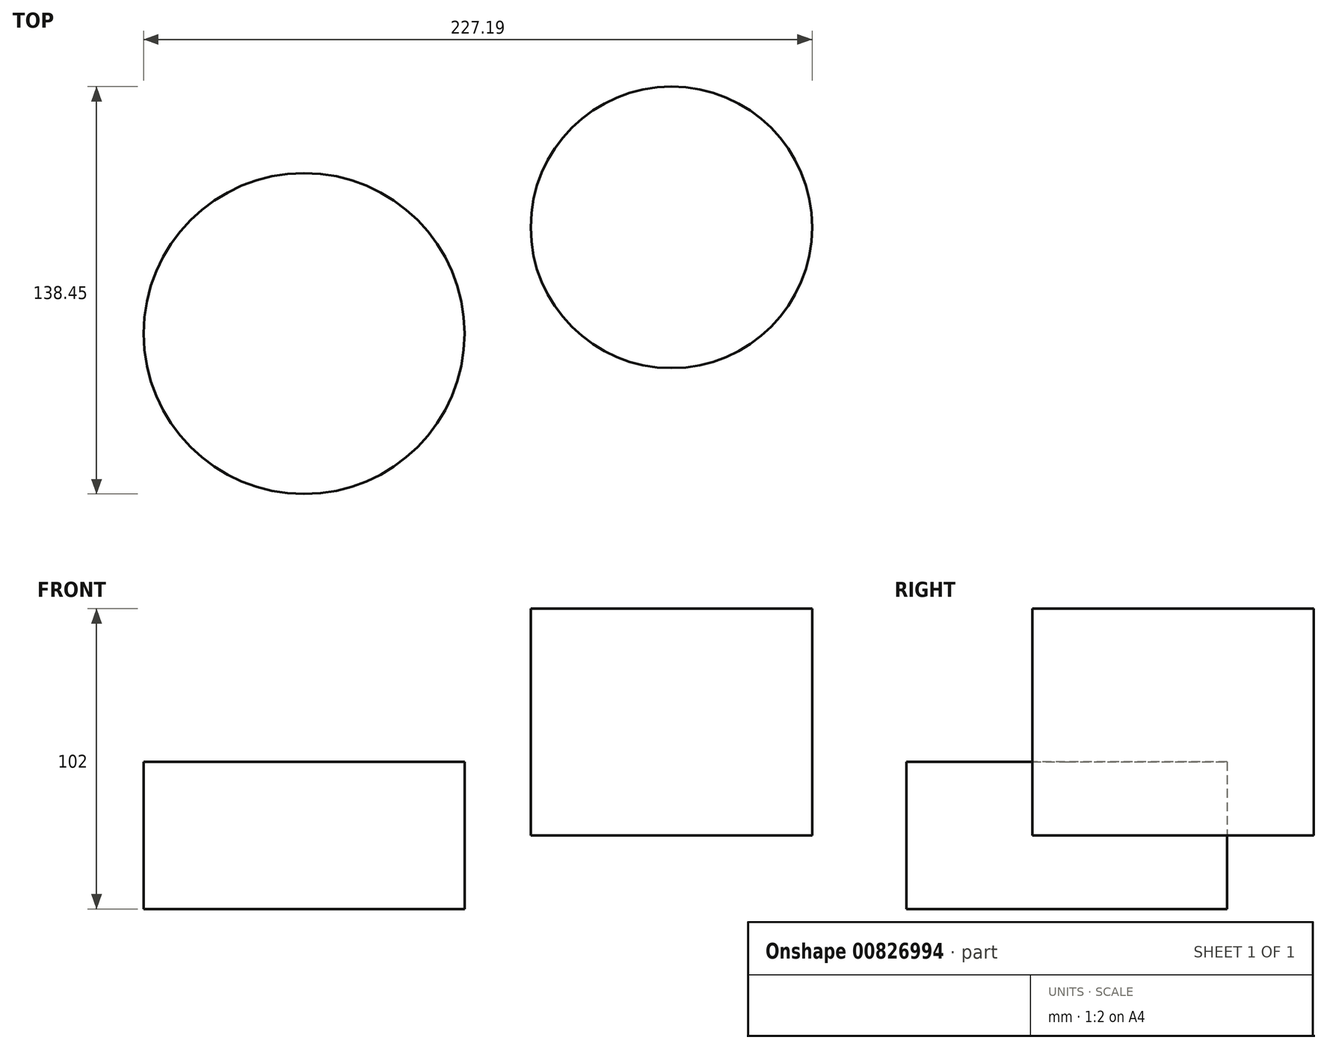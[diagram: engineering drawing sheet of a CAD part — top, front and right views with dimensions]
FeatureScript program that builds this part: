
annotation { "Feature Type Name" : "Feature", "Feature Type Description" : "" }
export const myFeature = defineFeature(function(context is Context, id is Id, definition is map)
    precondition{}
    {
        {
            var Q0;
            Q0=qCreatedBy(makeId("Top.planeOp"),FACE);
            var sketch = newSketch(context, id + "F0", { "sketchPlane" : qUnion([Q0])});
            skCircle(sketch, "E0", {"center": v(0, 0) * mm, "radius": 47.83 * mm});
            skSolve(sketch);
        }
        {
            var Q0;
            Q0=makeQuery(id+"F0.imprint","IMPRINT",FACE,{"disambiguationData":[TD([[makeQuery(id+"F0.imprint","IMPRINT",EDGE,{"derivedFrom":sQuery(id+"F0.wireOp",EDGE,"E0")}),1.0]])]});
            extrude(context, id + "F1", {"entities" : qUnion([Q0]), "depth" : 25 * mm, "offsetDistance" : 25 * mm});
        }
        {
            var Q0;
            Q0=qCreatedBy(makeId("Top.planeOp"),FACE);
            var sketch = newSketch(context, id + "F2", { "sketchPlane" : qUnion([Q0])});
            skCircle(sketch, "E1", {"center": v(-124.83, -36.1) * mm, "radius": 54.52 * mm});
            skSolve(sketch);
        }
        {
            var Q0;
            Q0=makeQuery(id+"F2.imprint","IMPRINT",FACE,{"disambiguationData":[TD([[makeQuery(id+"F2.imprint","IMPRINT",EDGE,{"derivedFrom":sQuery(id+"F2.wireOp",EDGE,"E1")}),1.0]])]});
            extrude(context, id + "F3", {"entities" : qUnion([Q0]), "depth" : 25 * mm, "offsetDistance" : 25 * mm});
        }
        {
            var Q0;
            Q0=makeQuery(id+"F3.opExtrude","CAP_FACE",FACE,{"disambiguationData":[OSD([sQuery(id+"F2.wireOp",EDGE,"E1")])],"isStart":false});
            extrude(context, id + "F4", {"entities" : qUnion([Q0]), "operationType" : NewBodyOperationType.ADD, "oppositeDirection" : true, "depth" : 25 * mm, "offsetDistance" : 25 * mm});
        }
        {
            var Q0;
            Q0=makeQuery(id+"F3.opExtrude","CAP_FACE",FACE,{"disambiguationData":[OSD([sQuery(id+"F2.wireOp",EDGE,"E1")])],"isStart":true});
            var Q1;
            Q1=makeQuery(id+"F3.opExtrude","CAP_FACE",FACE,{"disambiguationData":[OSD([sQuery(id+"F2.wireOp",EDGE,"E1")])],"isStart":false});
            extrude(context, id + "F5", {"entities" : qUnion([Q0, Q1]), "operationType" : NewBodyOperationType.ADD, "depth" : 25 * mm, "offsetDistance" : 25 * mm});
        }
        {
            var Q0;
            Q0=makeQuery(id+"F1.opExtrude","CAP_FACE",FACE,{"disambiguationData":[OSD([sQuery(id+"F0.wireOp",EDGE,"E0")])],"isStart":false});
            extrude(context, id + "F6", {"entities" : qUnion([Q0]), "operationType" : NewBodyOperationType.ADD, "depth" : 52 * mm, "offsetDistance" : 25 * mm});
        }
    });
